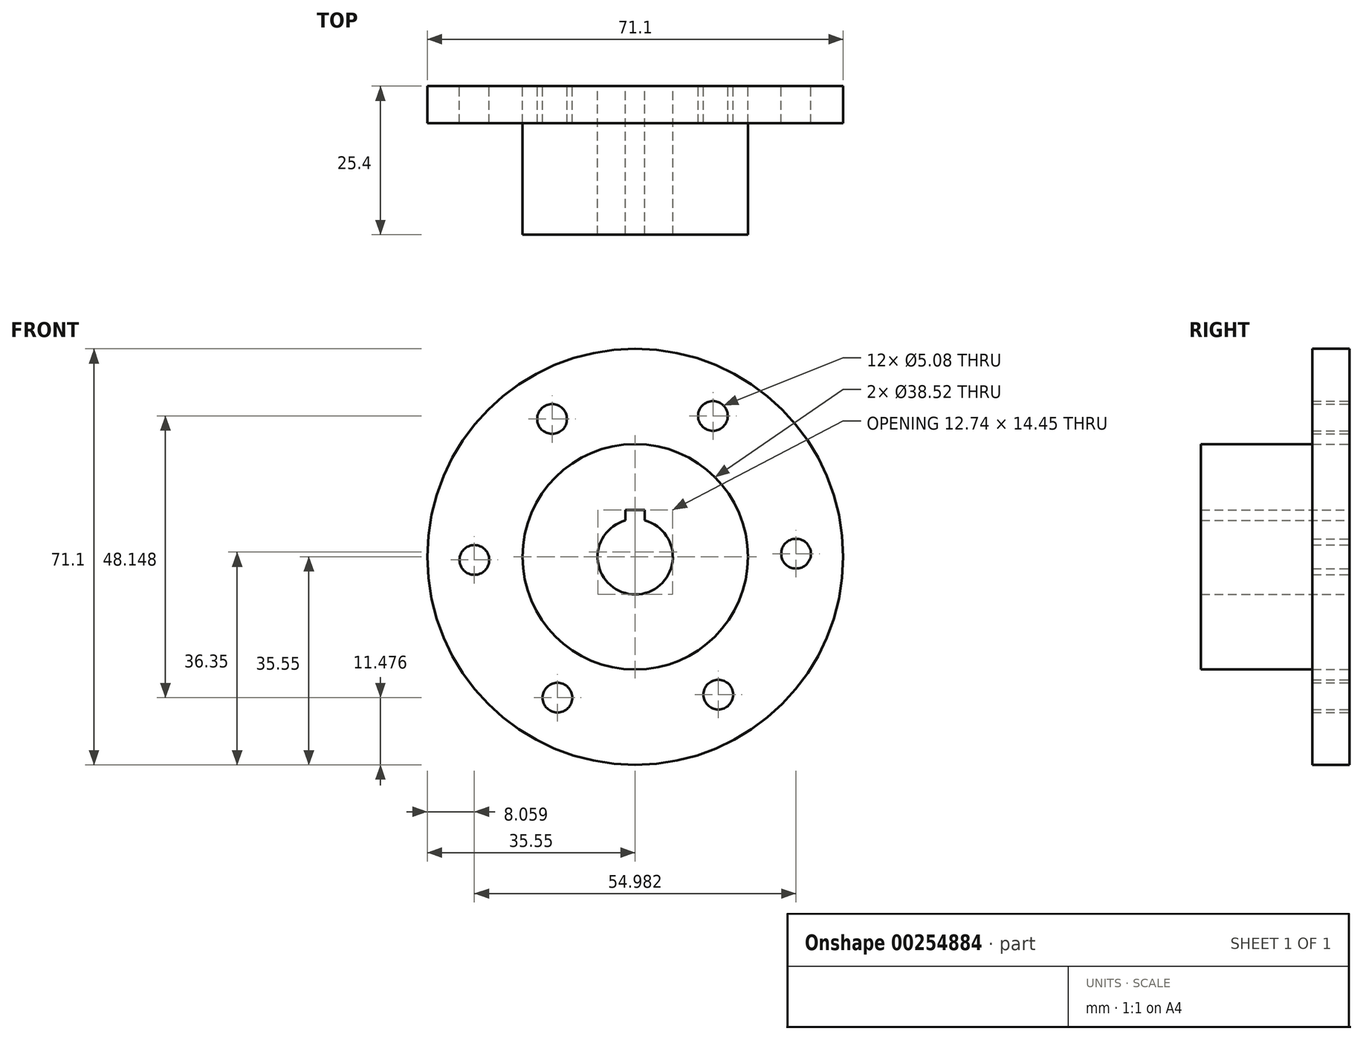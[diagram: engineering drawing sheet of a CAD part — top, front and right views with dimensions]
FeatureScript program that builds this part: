
annotation { "Feature Type Name" : "Feature", "Feature Type Description" : "" }
export const myFeature = defineFeature(function(context is Context, id is Id, definition is map)
    precondition{}
    {
        {
            var Q0;
            Q0=qCreatedBy(makeId("Front.planeOp"),FACE);
            var sketch = newSketch(context, id + "F0", { "sketchPlane" : qUnion([Q0])});
            skArc(sketch, "E0", {"start": v(-1.65, 6.21) * mm, "mid": v(0, -6.43) * mm, "end": v(1.65, 6.21) * mm});
            skLineSegment(sketch, "E1", {"start": v(-1.65, 6.21) * mm, "end": v(-1.65, 8.03) * mm});
            skLineSegment(sketch, "E2", {"start": v(1.65, 6.21) * mm, "end": v(1.65, 8.03) * mm});
            skLineSegment(sketch, "E3", {"start": v(1.65, 8.03) * mm, "end": v(-1.65, 8.03) * mm});
            skCircle(sketch, "E4", {"center": v(0, 0) * mm, "radius": 12.2 * mm});
            skCircle(sketch, "E5", {"center": v(0, 0) * mm, "radius": 19.26 * mm});
            skCircle(sketch, "E6", {"center": v(0, 0) * mm, "radius": 35.55 * mm});
            skLineSegment(sketch, "E7.0", {"start": v(-13.28, -24.07) * mm, "end": v(-14.6, -21.9) * mm});
            skLineSegment(sketch, "E7.2", {"start": v(-14.2, 23.54) * mm, "end": v(-11.67, 23.6) * mm});
            skLineSegment(sketch, "E7.3", {"start": v(13.28, 24.07) * mm, "end": v(14.6, 21.9) * mm});
            skLineSegment(sketch, "E7.4", {"start": v(27.5, 0.53) * mm, "end": v(26.26, -1.7) * mm});
            skLineSegment(sketch, "E7.5", {"start": v(14.2, -23.54) * mm, "end": v(11.67, -23.6) * mm});
            skPoint(sketch, "E7.0.midPoint", {"position": v(-20.39, -12.3) * mm});
            skCircle(sketch, "E8", {"center": v(-14.2, 23.54) * mm, "radius": 2.54 * mm});
            skCircle(sketch, "E9", {"center": v(13.28, 24.07) * mm, "radius": 2.54 * mm});
            skCircle(sketch, "E10", {"center": v(-27.5, -0.53) * mm, "radius": 2.54 * mm});
            skCircle(sketch, "E11", {"center": v(-13.28, -24.07) * mm, "radius": 2.54 * mm});
            skCircle(sketch, "E12", {"center": v(14.2, -23.54) * mm, "radius": 2.54 * mm});
            skCircle(sketch, "E13", {"center": v(27.5, 0.53) * mm, "radius": 2.54 * mm});
            skArc(sketch, "E14.trimOffspring", {"start": v(-12.7, 25.6) * mm, "mid": v(-14.76, 24.47) * mm, "end": v(-16.72, 23.17) * mm});
            skArc(sketch, "E15.trimOffspring", {"start": v(15.81, 23.8) * mm, "mid": v(13.8, 25.02) * mm, "end": v(11.7, 26.07) * mm});
            skArc(sketch, "E16.trimOffspring", {"start": v(28.52, -1.8) * mm, "mid": v(28.57, 0.55) * mm, "end": v(28.43, 2.9) * mm});
            skArc(sketch, "E17.trimOffspring", {"start": v(12.7, -25.6) * mm, "mid": v(14.76, -24.47) * mm, "end": v(16.72, -23.17) * mm});
            skArc(sketch, "E18.trimOffspring", {"start": v(-15.81, -23.8) * mm, "mid": v(-13.8, -25.02) * mm, "end": v(-11.7, -26.07) * mm});
            skLineSegment(sketch, "E19.trimOffspring", {"start": v(-15.43, 21.32) * mm, "end": v(-14.2, 23.54) * mm});
            skLineSegment(sketch, "E20.trimOffspring", {"start": v(10.75, 24.02) * mm, "end": v(13.28, 24.07) * mm});
            skLineSegment(sketch, "E21.trimOffspring", {"start": v(26.18, 2.7) * mm, "end": v(27.5, 0.53) * mm});
            skLineSegment(sketch, "E22.trimOffspring", {"start": v(15.43, -21.32) * mm, "end": v(14.2, -23.54) * mm});
            skLineSegment(sketch, "E23.trimOffspring", {"start": v(-10.75, -24.02) * mm, "end": v(-13.28, -24.07) * mm});
            skSolve(sketch);
        }
        {
            var Q0;
            Q0=makeQuery(id+"F0.imprint","IMPRINT",FACE,{"disambiguationData":[TD([[makeQuery(id+"F0.imprint","IMPRINT",EDGE,{"derivedFrom":sQuery(id+"F0.wireOp",EDGE,"E4")}),-1.0]])]});
            var Q1;
            Q1=makeQuery(id+"F0.imprint","IMPRINT",FACE,{"disambiguationData":[TD([[makeQuery(id+"F0.imprint","IMPRINT",EDGE,{"derivedFrom":sQuery(id+"F0.wireOp",EDGE,"E0")}),-1.0]])]});
            extrude(context, id + "F1", {"entities" : qUnion([Q0, Q1]), "depth" : 25.4 * mm});
        }
        {
            var Q0;
            Q0=makeQuery(id+"F0.imprint","IMPRINT",FACE,{"disambiguationData":[TD([[makeQuery(id+"F0.imprint","IMPRINT",EDGE,{"derivedFrom":sQuery(id+"F0.wireOp",EDGE,"E6")}),1.0]])]});
            extrude(context, id + "F2", {"entities" : qUnion([Q0]), "depth" : 6.35 * mm});
        }
        {
            var Q0;
            Q0=makeQuery(id+"F0.imprint","IMPRINT",FACE,{"disambiguationData":[TD([[makeQuery(id+"F0.imprint","IMPRINT",EDGE,{"derivedFrom":sQuery(id+"F0.wireOp",EDGE,"E5")}),-1.0]])]});
            var Q1;
            {var subQ0=sQuery(id+"F0.wireOp",EDGE,"E10");var subQ1=sQuery(id+"F0.wireOp",EDGE,"mVgpZlDX-BBfQ-FZ9L-0dvA-47XcTVDPdtow");var subQ2=makeQuery(id+"F0.imprint","INTERSECT",VERTEX,{"disambiguationData":[OD(1.0)],"derivedFrom":[subQ1,subQ0]});Q1=makeQuery(id+"F0.imprint","IMPRINT",FACE,{"disambiguationData":[TD([[makeQuery(id+"F0.imprint","IMPRINT",EDGE,{"disambiguationData":[TD([[subQ2,-1.0]])],"derivedFrom":subQ1}),1.0]])]});}
            var Q2;
            {var subQ0=sQuery(id+"F0.wireOp",EDGE,"E8");var subQ1=sQuery(id+"F0.wireOp",EDGE,"mVgpZlDX-BBfQ-FZ9L-0dvA-47XcTVDPdtow");var subQ2=makeQuery(id+"F0.imprint","INTERSECT",VERTEX,{"disambiguationData":[OD(1.0)],"derivedFrom":[subQ1,subQ0]});Q2=makeQuery(id+"F0.imprint","IMPRINT",FACE,{"disambiguationData":[TD([[makeQuery(id+"F0.imprint","IMPRINT",EDGE,{"disambiguationData":[TD([[subQ2,-1.0]])],"derivedFrom":subQ1}),1.0]])]});}
            var Q3;
            {var subQ0=sQuery(id+"F0.wireOp",EDGE,"E11");var subQ1=sQuery(id+"F0.wireOp",EDGE,"mVgpZlDX-BBfQ-FZ9L-0dvA-47XcTVDPdtow");var subQ2=makeQuery(id+"F0.imprint","INTERSECT",VERTEX,{"disambiguationData":[OD(1.0)],"derivedFrom":[subQ1,subQ0]});Q3=makeQuery(id+"F0.imprint","IMPRINT",FACE,{"disambiguationData":[TD([[makeQuery(id+"F0.imprint","IMPRINT",EDGE,{"disambiguationData":[TD([[subQ2,-1.0]])],"derivedFrom":subQ1}),1.0]])]});}
            var Q4;
            {var subQ0=sQuery(id+"F0.wireOp",EDGE,"E12");var subQ1=sQuery(id+"F0.wireOp",EDGE,"mVgpZlDX-BBfQ-FZ9L-0dvA-47XcTVDPdtow");var subQ2=makeQuery(id+"F0.imprint","INTERSECT",VERTEX,{"disambiguationData":[OD(1.0)],"derivedFrom":[subQ1,subQ0]});Q4=makeQuery(id+"F0.imprint","IMPRINT",FACE,{"disambiguationData":[TD([[makeQuery(id+"F0.imprint","IMPRINT",EDGE,{"disambiguationData":[TD([[subQ2,-1.0]])],"derivedFrom":subQ1}),1.0]])]});}
            var Q5;
            {var subQ0=sQuery(id+"F0.wireOp",EDGE,"E9");var subQ1=sQuery(id+"F0.wireOp",EDGE,"mVgpZlDX-BBfQ-FZ9L-0dvA-47XcTVDPdtow");var subQ2=makeQuery(id+"F0.imprint","INTERSECT",VERTEX,{"disambiguationData":[OD(0.0)],"derivedFrom":[subQ1,subQ0]});Q5=makeQuery(id+"F0.imprint","IMPRINT",FACE,{"disambiguationData":[TD([[makeQuery(id+"F0.imprint","IMPRINT",EDGE,{"disambiguationData":[TD([[subQ2,1.0]])],"derivedFrom":subQ1}),1.0]])]});}
            var Q6;
            {var subQ0=sQuery(id+"F0.wireOp",EDGE,"E9");var subQ1=sQuery(id+"F0.wireOp",EDGE,"mVgpZlDX-BBfQ-FZ9L-0dvA-47XcTVDPdtow");var subQ2=makeQuery(id+"F0.imprint","INTERSECT",VERTEX,{"disambiguationData":[OD(1.0)],"derivedFrom":[subQ1,subQ0]});Q6=makeQuery(id+"F0.imprint","IMPRINT",FACE,{"disambiguationData":[TD([[makeQuery(id+"F0.imprint","IMPRINT",EDGE,{"disambiguationData":[TD([[subQ2,-1.0]])],"derivedFrom":subQ1}),1.0]])]});}
            extrude(context, id + "F3", {"entities" : qUnion([Q0, Q1, Q2, Q3, Q4, Q5, Q6]), "depth" : 6.35 * mm});
        }
    });
